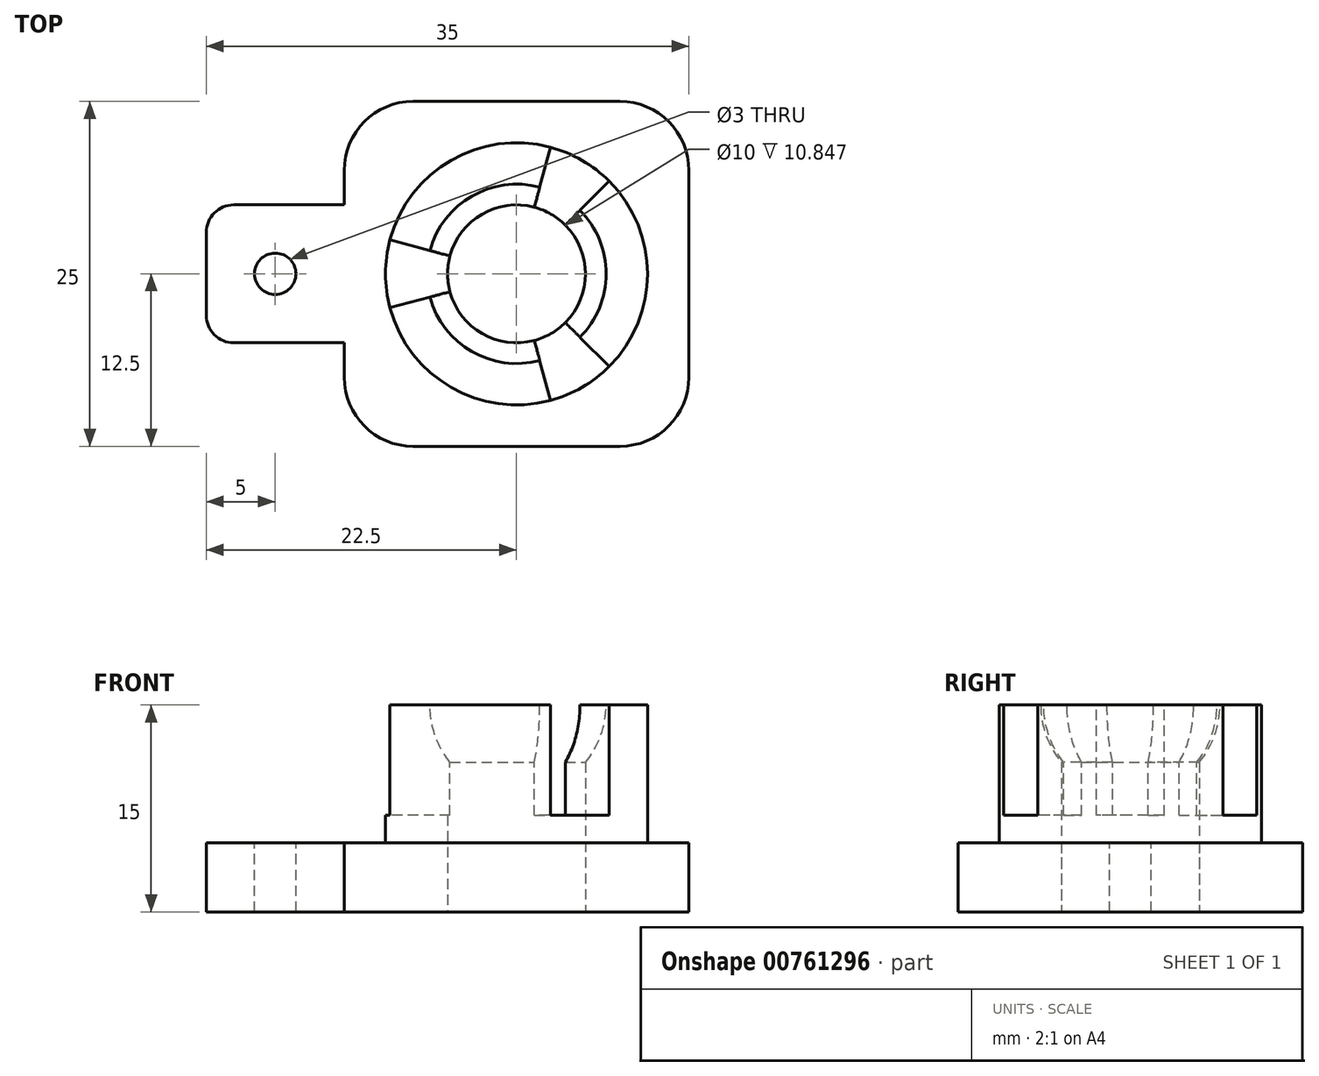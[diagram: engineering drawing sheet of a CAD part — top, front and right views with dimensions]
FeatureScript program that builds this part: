
annotation { "Feature Type Name" : "Feature", "Feature Type Description" : "" }
export const myFeature = defineFeature(function(context is Context, id is Id, definition is map)
    precondition{}
    {
        {
            var Q0;
            Q0=qCreatedBy(makeId("Top.planeOp"),FACE);
            var sketch = newSketch(context, id + "F0", { "sketchPlane" : qUnion([Q0])});
            skLineSegment(sketch, "E0.bottom", {"start": v(-7.5, 12.5) * mm, "end": v(0, 12.5) * mm});
            skLineSegment(sketch, "E0.top", {"start": v(-7.5, -12.5) * mm, "end": v(0, -12.5) * mm});
            skLineSegment(sketch, "E0.left", {"start": v(-12.5, 7.5) * mm, "end": v(-12.5, -7.5) * mm});
            skPoint(sketch, "E0.middle", {"position": v(0, 0) * mm});
            skLineSegment(sketch, "E1.bottom", {"start": v(-20.5, 5) * mm, "end": v(-12.5, 5) * mm});
            skLineSegment(sketch, "E1.top", {"start": v(-20.5, -5) * mm, "end": v(-12.5, -5) * mm});
            skLineSegment(sketch, "E1.left", {"start": v(-22.5, 3) * mm, "end": v(-22.5, -3) * mm});
            skPoint(sketch, "E1.middle", {"position": v(-12.5, 0) * mm});
            skPoint(sketch, "E2.visualSharp", {"position": v(-12.5, 12.5) * mm});
            skArc(sketch, "E2.filletArc", {"start": v(-7.5, 12.5) * mm, "mid": v(-11.04, 11.04) * mm, "end": v(-12.5, 7.5) * mm});
            skPoint(sketch, "E3.visualSharp", {"position": v(-12.5, -12.5) * mm});
            skArc(sketch, "E3.filletArc", {"start": v(-12.5, -7.5) * mm, "mid": v(-11.04, -11.04) * mm, "end": v(-7.5, -12.5) * mm});
            skPoint(sketch, "E4.visualSharp", {"position": v(-22.5, 5) * mm});
            skArc(sketch, "E4.filletArc", {"start": v(-20.5, 5) * mm, "mid": v(-21.91, 4.41) * mm, "end": v(-22.5, 3) * mm});
            skPoint(sketch, "E5.visualSharp", {"position": v(-22.5, -5) * mm});
            skArc(sketch, "E5.filletArc", {"start": v(-22.5, -3) * mm, "mid": v(-21.91, -4.41) * mm, "end": v(-20.5, -5) * mm});
            skArc(sketch, "E6.MirrorCS", {"start": v(22.5, -3) * mm, "mid": v(21.91, -4.41) * mm, "end": v(20.5, -5) * mm});
            skArc(sketch, "E7.MirrorCS", {"start": v(20.5, 5) * mm, "mid": v(21.91, 4.41) * mm, "end": v(22.5, 3) * mm});
            skLineSegment(sketch, "E8.MirrorCS", {"start": v(7.5, 12.5) * mm, "end": v(0, 12.5) * mm});
            skPoint(sketch, "E9.MirrorP", {"position": v(12.5, 0) * mm});
            skPoint(sketch, "E10.MirrorP", {"position": v(22.5, 5) * mm});
            skArc(sketch, "E11.MirrorCS", {"start": v(7.5, 12.5) * mm, "mid": v(11.04, 11.04) * mm, "end": v(12.5, 7.5) * mm});
            skArc(sketch, "E12.MirrorCS", {"start": v(12.5, -7.5) * mm, "mid": v(11.04, -11.04) * mm, "end": v(7.5, -12.5) * mm});
            skLineSegment(sketch, "E13.MirrorCS", {"start": v(22.5, 3) * mm, "end": v(22.5, -3) * mm});
            skLineSegment(sketch, "E14.MirrorCS", {"start": v(20.5, 5) * mm, "end": v(12.5, 5) * mm});
            skLineSegment(sketch, "E15.MirrorCS", {"start": v(7.5, -12.5) * mm, "end": v(0, -12.5) * mm});
            skPoint(sketch, "E16.MirrorP", {"position": v(22.5, -5) * mm});
            skLineSegment(sketch, "E17.MirrorCS", {"start": v(20.5, -5) * mm, "end": v(12.5, -5) * mm});
            skLineSegment(sketch, "E18.MirrorCS", {"start": v(12.5, 7.5) * mm, "end": v(12.5, -7.5) * mm});
            skPoint(sketch, "E19.MirrorP", {"position": v(12.5, -12.5) * mm});
            skPoint(sketch, "E20.MirrorP", {"position": v(12.5, 12.5) * mm});
            skLineSegment(sketch, "E21", {"start": v(0, 19.67) * mm, "end": v(0, -21.46) * mm, "construction": true});
            skSolve(sketch);
        }
        {
            var Q0;
            {var subQ1=sQuery(id+"F0.wireOp",EDGE,"E1.bottom");Q0=makeQuery(id+"F0.imprint","IMPRINT",FACE,{"disambiguationData":[TD([[makeQuery(id+"F0.imprint","IMPRINT",EDGE,{"derivedFrom":subQ1}),-1.0]])]});}
            var Q1;
            Q1=makeQuery(id+"F0.imprint","IMPRINT",FACE,{"disambiguationData":[TD([[makeQuery(id+"F0.imprint","IMPRINT",EDGE,{"derivedFrom":sQuery(id+"F0.wireOp",EDGE,"E0.bottom")}),-1.0]])]});
            var Q2;
            Q2=makeQuery(id+"F0.imprint","IMPRINT",FACE,{"disambiguationData":[TD([[makeQuery(id+"F0.imprint","IMPRINT",EDGE,{"derivedFrom":sQuery(id+"F0.wireOp",EDGE,"E6.MirrorCS")}),-1.0]])]});
            extrude(context, id + "F1", {"entities" : qUnion([Q0, Q1, Q2]), "depth" : 5 * mm, "offsetDistance" : 25 * mm});
        }
        {
            var Q0;
            Q0=makeQuery(id+"F1.opExtrude","CAP_FACE",FACE,{"disambiguationData":[OSD([sQuery(id+"F0.wireOp",EDGE,"E0.bottom"),sQuery(id+"F0.wireOp",EDGE,"E0.top"),sQuery(id+"F0.wireOp",EDGE,"E0.left"),sQuery(id+"F0.wireOp",EDGE,"E1.bottom"),sQuery(id+"F0.wireOp",EDGE,"E1.top"),sQuery(id+"F0.wireOp",EDGE,"E1.left"),sQuery(id+"F0.wireOp",EDGE,"E2.filletArc"),sQuery(id+"F0.wireOp",EDGE,"E3.filletArc"),sQuery(id+"F0.wireOp",EDGE,"E4.filletArc"),sQuery(id+"F0.wireOp",EDGE,"E5.filletArc"),sQuery(id+"F0.wireOp",EDGE,"E6.MirrorCS"),sQuery(id+"F0.wireOp",EDGE,"E7.MirrorCS"),sQuery(id+"F0.wireOp",EDGE,"E8.MirrorCS"),sQuery(id+"F0.wireOp",EDGE,"E11.MirrorCS"),sQuery(id+"F0.wireOp",EDGE,"E12.MirrorCS"),sQuery(id+"F0.wireOp",EDGE,"E13.MirrorCS"),sQuery(id+"F0.wireOp",EDGE,"E14.MirrorCS"),sQuery(id+"F0.wireOp",EDGE,"E15.MirrorCS"),sQuery(id+"F0.wireOp",EDGE,"E17.MirrorCS"),sQuery(id+"F0.wireOp",EDGE,"E18.MirrorCS")])],"isStart":false});
            var sketch = newSketch(context, id + "F2", { "sketchPlane" : qUnion([Q0])});
            skCircle(sketch, "E22", {"center": v(-17.5, 0) * mm, "radius": 1.5 * mm});
            skLineSegment(sketch, "E23", {"start": v(0, 12.5) * mm, "end": v(0, -12.5) * mm, "construction": true});
            skCircle(sketch, "E24.MirrorC", {"center": v(17.5, 0) * mm, "radius": 1.5 * mm});
            skLineSegment(sketch, "E25", {"start": v(-17.5, 0) * mm, "end": v(17.5, 0) * mm, "construction": true});
            skCircle(sketch, "E26", {"center": v(0, 0) * mm, "radius": 6.5 * mm});
            skCircle(sketch, "E27.0", {"center": v(0, 0) * mm, "radius": 9.5 * mm});
            skSolve(sketch);
        }
        {
            var Q0;
            Q0=sQuery(id+"F2.wireOp",VERTEX,"E22.center");
            var Q1;
            Q1=makeQuery(id+"F1.opExtrude","SWEPT_BODY",BODY,{"disambiguationData":[OSD([sQuery(id+"F0.wireOp",EDGE,"E0.bottom"),sQuery(id+"F0.wireOp",EDGE,"E0.top"),sQuery(id+"F0.wireOp",EDGE,"E0.left"),sQuery(id+"F0.wireOp",EDGE,"E1.bottom"),sQuery(id+"F0.wireOp",EDGE,"E1.top"),sQuery(id+"F0.wireOp",EDGE,"E1.left"),sQuery(id+"F0.wireOp",EDGE,"E2.filletArc"),sQuery(id+"F0.wireOp",EDGE,"E3.filletArc"),sQuery(id+"F0.wireOp",EDGE,"E4.filletArc"),sQuery(id+"F0.wireOp",EDGE,"E5.filletArc"),sQuery(id+"F0.wireOp",EDGE,"E6.MirrorCS"),sQuery(id+"F0.wireOp",EDGE,"E7.MirrorCS"),sQuery(id+"F0.wireOp",EDGE,"E8.MirrorCS"),sQuery(id+"F0.wireOp",EDGE,"E11.MirrorCS"),sQuery(id+"F0.wireOp",EDGE,"E12.MirrorCS"),sQuery(id+"F0.wireOp",EDGE,"E13.MirrorCS"),sQuery(id+"F0.wireOp",EDGE,"E14.MirrorCS"),sQuery(id+"F0.wireOp",EDGE,"E15.MirrorCS"),sQuery(id+"F0.wireOp",EDGE,"E17.MirrorCS"),sQuery(id+"F0.wireOp",EDGE,"E18.MirrorCS")])]});
            hole(context, id + "F3", {"style" : HoleStyle.SIMPLE, "endStyle" : HoleEndStyle.THROUGH, "holeDiameter" : 3 * mm, "majorDiameter" : 5 * mm, "isTappedThrough" : true, "tappedDepth" : 12 * mm, "tapClearance" : 3, "startFromSketch" : true, "locations" : qUnion([Q0]), "scope" : qUnion([Q1])});
        }
        {
            var Q0;
            Q0=sQuery(id+"F2.wireOp",VERTEX,"E24.MirrorC.center");
            var Q1;
            Q1=makeQuery(id+"F1.opExtrude","SWEPT_BODY",BODY,{"disambiguationData":[OSD([sQuery(id+"F0.wireOp",EDGE,"E0.bottom"),sQuery(id+"F0.wireOp",EDGE,"E0.top"),sQuery(id+"F0.wireOp",EDGE,"E0.left"),sQuery(id+"F0.wireOp",EDGE,"E1.bottom"),sQuery(id+"F0.wireOp",EDGE,"E1.top"),sQuery(id+"F0.wireOp",EDGE,"E1.left"),sQuery(id+"F0.wireOp",EDGE,"E2.filletArc"),sQuery(id+"F0.wireOp",EDGE,"E3.filletArc"),sQuery(id+"F0.wireOp",EDGE,"E4.filletArc"),sQuery(id+"F0.wireOp",EDGE,"E5.filletArc"),sQuery(id+"F0.wireOp",EDGE,"E6.MirrorCS"),sQuery(id+"F0.wireOp",EDGE,"E7.MirrorCS"),sQuery(id+"F0.wireOp",EDGE,"E8.MirrorCS"),sQuery(id+"F0.wireOp",EDGE,"E11.MirrorCS"),sQuery(id+"F0.wireOp",EDGE,"E12.MirrorCS"),sQuery(id+"F0.wireOp",EDGE,"E13.MirrorCS"),sQuery(id+"F0.wireOp",EDGE,"E14.MirrorCS"),sQuery(id+"F0.wireOp",EDGE,"E15.MirrorCS"),sQuery(id+"F0.wireOp",EDGE,"E17.MirrorCS"),sQuery(id+"F0.wireOp",EDGE,"E18.MirrorCS")])]});
            hole(context, id + "F4", {"style" : HoleStyle.SIMPLE, "endStyle" : HoleEndStyle.THROUGH, "holeDiameter" : 3 * mm, "majorDiameter" : 5 * mm, "isTappedThrough" : true, "tappedDepth" : 12 * mm, "tapClearance" : 3, "startFromSketch" : true, "locations" : qUnion([Q0]), "scope" : qUnion([Q1])});
        }
        {
            var Q0;
            Q0=makeQuery(id+"F2.imprint","IMPRINT",FACE,{"disambiguationData":[TD([[makeQuery(id+"F2.imprint","IMPRINT",EDGE,{"derivedFrom":sQuery(id+"F2.wireOp",EDGE,"E26")}),1.0]])]});
            var Q1;
            Q1=makeQuery(id+"F2.imprint","IMPRINT",FACE,{"disambiguationData":[TD([[makeQuery(id+"F2.imprint","IMPRINT",EDGE,{"derivedFrom":sQuery(id+"F2.wireOp",EDGE,"E26")}),-1.0]])]});
            extrude(context, id + "F5", {"entities" : qUnion([Q0, Q1]), "operationType" : NewBodyOperationType.ADD, "depth" : 10 * mm, "offsetDistance" : 25 * mm});
        }
        {
            var Q0;
            Q0=makeQuery(id+"F5.opExtrude","CAP_FACE",FACE,{"disambiguationData":[OSD([sQuery(id+"F2.wireOp",EDGE,"E27.0")])],"isStart":false});
            var sketch = newSketch(context, id + "F6", { "sketchPlane" : qUnion([Q0])});
            skLineSegment(sketch, "E28", {"start": v(-4.83, 1.3) * mm, "end": v(-9.18, 2.46) * mm});
            skLineSegment(sketch, "E29.MirrorCS", {"start": v(-4.83, -1.3) * mm, "end": v(-9.18, -2.46) * mm});
            skPoint(sketch, "E30.orphan", {"position": v(0, 0) * mm});
            skArc(sketch, "E31", {"start": v(-9.18, 2.46) * mm, "mid": v(-9.5, 0) * mm, "end": v(-9.18, -2.46) * mm});
            skArc(sketch, "E32", {"start": v(-4.83, 1.3) * mm, "mid": v(-5, 0) * mm, "end": v(-4.83, -1.3) * mm});
            skArc(sketch, "E33.1.0", {"start": v(2.46, -9.18) * mm, "mid": v(4.75, -8.23) * mm, "end": v(6.72, -6.72) * mm});
            skLineSegment(sketch, "E33.1.1", {"start": v(1.3, -4.83) * mm, "end": v(2.46, -9.18) * mm});
            skArc(sketch, "E33.1.2", {"start": v(1.3, -4.83) * mm, "mid": v(2.5, -4.33) * mm, "end": v(3.54, -3.54) * mm});
            skLineSegment(sketch, "E33.1.3", {"start": v(3.54, -3.54) * mm, "end": v(6.72, -6.72) * mm});
            skArc(sketch, "E33.2.0", {"start": v(6.72, 6.72) * mm, "mid": v(4.75, 8.23) * mm, "end": v(2.46, 9.18) * mm});
            skLineSegment(sketch, "E33.2.1", {"start": v(3.54, 3.54) * mm, "end": v(6.72, 6.72) * mm});
            skArc(sketch, "E33.2.2", {"start": v(3.54, 3.54) * mm, "mid": v(2.5, 4.33) * mm, "end": v(1.3, 4.83) * mm});
            skLineSegment(sketch, "E33.2.3", {"start": v(1.3, 4.83) * mm, "end": v(2.46, 9.18) * mm});
            skSolve(sketch);
        }
        {
            var Q0;
            Q0 = qSketchRegion(id + "F6", true);
            extrude(context, id + "F7", {"entities" : qUnion([Q0]), "operationType" : NewBodyOperationType.REMOVE, "oppositeDirection" : true, "depth" : 8 * mm, "offsetDistance" : 25 * mm});
        }
        {
            var Q0;
            {var subQ3=sQuery(id+"F6.wireOp",EDGE,"E28");Q0=makeQuery(id+"F6.imprint","IMPRINT",FACE,{"disambiguationData":[TD([[makeQuery(id+"F6.imprint","IMPRINT",EDGE,{"derivedFrom":subQ3}),-1.0]])]});}
            var sketch = newSketch(context, id + "F8", { "sketchPlane" : qUnion([Q0])});
            skArc(sketch, "E34", {"start": v(6.5, 0) * mm, "mid": v(0, 6.5) * mm, "end": v(-6.5, 0) * mm});
            skLineSegment(sketch, "E35", {"start": v(-6.5, 0) * mm, "end": v(6.5, 0) * mm});
            skSolve(sketch);
        }
        {
            var Q0;
            {var subQ0=sQuery(id+"F8.wireOp",EDGE,"E35");var subQ1=sQuery(id+"F8.wireOp",EDGE,"E34");var subQ2=makeQuery(id+"F8.imprint","INTERSECT",VERTEX,{"disambiguationData":[OD(1.0)],"derivedFrom":[subQ1,subQ0]});Q0=makeQuery(id+"F8.imprint","IMPRINT",FACE,{"disambiguationData":[TD([[makeQuery(id+"F8.imprint","IMPRINT",EDGE,{"disambiguationData":[TD([[subQ2,1.0]])],"derivedFrom":subQ1}),1.0]])]});}
            var Q1;
            {var subQ5=makeQuery(id+"F6.imprint","IMPRINT",EDGE,{"derivedFrom":sQuery(id+"F6.wireOp",EDGE,"E33.2.2")});Q1=makeQuery(id+"F8.imprint","IMPRINT",FACE,{"disambiguationData":[TD([[makeQuery(id+"F8.imprint","IMPRINT",EDGE,{"derivedFrom":subQ5}),1.0]])]});}
            var Q2;
            {var subQ5=makeQuery(id+"F6.imprint","IMPRINT",EDGE,{"derivedFrom":sQuery(id+"F6.wireOp",EDGE,"E33.2.2")});Q2=makeQuery(id+"F8.imprint","IMPRINT",FACE,{"disambiguationData":[TD([[makeQuery(id+"F8.imprint","IMPRINT",EDGE,{"derivedFrom":subQ5}),-1.0]])]});}
            var Q3;
            Q3=sQuery(id+"F8.wireOp",EDGE,"E35");
            revolve(context, id + "F9", {"operationType" : NewBodyOperationType.REMOVE, "surfaceOperationType" : NewSurfaceOperationType.NEW, "entities" : qUnion([Q0, Q1, Q2]), "axis" : qUnion([Q3]), "revolveType" : RevolveType.ONE_DIRECTION, "oppositeDirection" : true, "angle" : 180 * degree});
        }
        {
            var Q0;
            Q0=makeQuery(id+"F1.opExtrude","CAP_FACE",FACE,{"disambiguationData":[OSD([sQuery(id+"F0.wireOp",EDGE,"E0.bottom"),sQuery(id+"F0.wireOp",EDGE,"E0.top"),sQuery(id+"F0.wireOp",EDGE,"E0.left"),sQuery(id+"F0.wireOp",EDGE,"E1.bottom"),sQuery(id+"F0.wireOp",EDGE,"E1.top"),sQuery(id+"F0.wireOp",EDGE,"E1.left"),sQuery(id+"F0.wireOp",EDGE,"E2.filletArc"),sQuery(id+"F0.wireOp",EDGE,"E3.filletArc"),sQuery(id+"F0.wireOp",EDGE,"E4.filletArc"),sQuery(id+"F0.wireOp",EDGE,"E5.filletArc"),sQuery(id+"F0.wireOp",EDGE,"E6.MirrorCS"),sQuery(id+"F0.wireOp",EDGE,"E7.MirrorCS"),sQuery(id+"F0.wireOp",EDGE,"E8.MirrorCS"),sQuery(id+"F0.wireOp",EDGE,"E11.MirrorCS"),sQuery(id+"F0.wireOp",EDGE,"E12.MirrorCS"),sQuery(id+"F0.wireOp",EDGE,"E13.MirrorCS"),sQuery(id+"F0.wireOp",EDGE,"E14.MirrorCS"),sQuery(id+"F0.wireOp",EDGE,"E15.MirrorCS"),sQuery(id+"F0.wireOp",EDGE,"E17.MirrorCS"),sQuery(id+"F0.wireOp",EDGE,"E18.MirrorCS")])],"isStart":true});
            var sketch = newSketch(context, id + "F10", { "sketchPlane" : qUnion([Q0])});
            skCircle(sketch, "E36", {"center": v(0, 0) * mm, "radius": 5 * mm});
            skSolve(sketch);
        }
        {
            var Q0;
            Q0=makeQuery(id+"F10.imprint","IMPRINT",FACE,{"disambiguationData":[TD([[makeQuery(id+"F10.imprint","IMPRINT",EDGE,{"derivedFrom":sQuery(id+"F10.wireOp",EDGE,"E36")}),1.0]])]});
            extrude(context, id + "F11", {"entities" : qUnion([Q0]), "operationType" : NewBodyOperationType.REMOVE, "oppositeDirection" : true, "depth" : 25 * mm, "offsetDistance" : 25 * mm});
        }
    });
